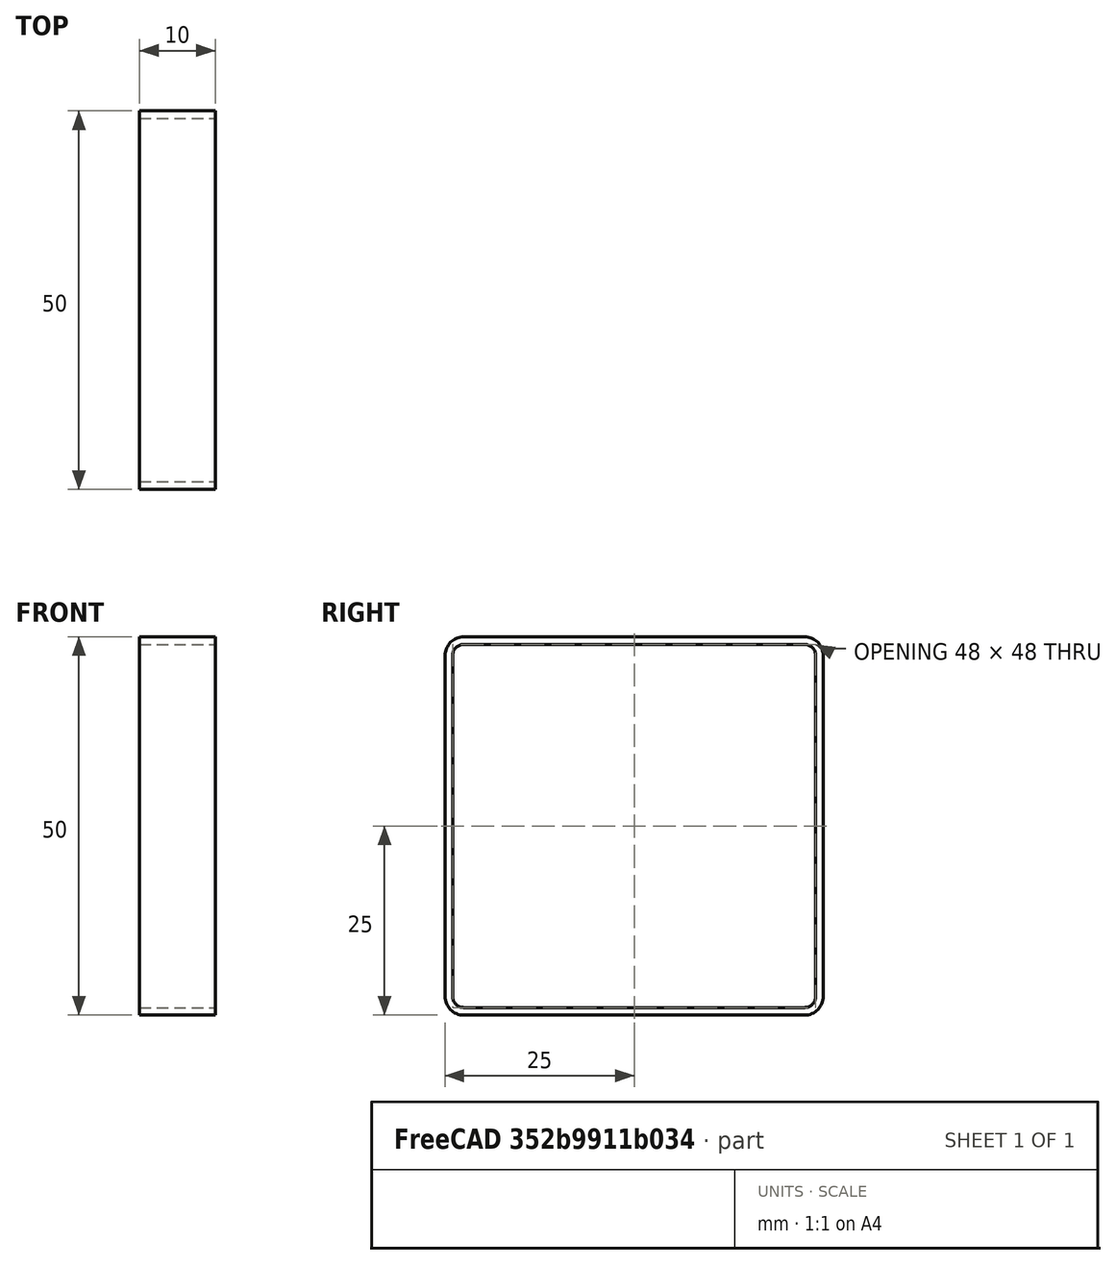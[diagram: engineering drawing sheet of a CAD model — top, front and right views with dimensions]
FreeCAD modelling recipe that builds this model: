
FCSTD DOCUMENT  (FreeCAD 0.20R26075 +2 (Git))
Label: Test6
License: All rights reserved
LicenseURL: http://en.wikipedia.org/wiki/All_rights_reserved
objects: Sketcher::SketchObject×1, PartDesign::Pad×1, PartDesign::Body×1
note: 4 computed .brp shape members not serialized (recipe doc carries the construction recipe); baked Part::Feature solids carry a one-line shape summary decoded from their .brp

FEATURE [Sketcher::SketchObject] Sketch
  FullyConstrained = true
  MapMode = 5
  Placement = pos=(0,0,0) rot=(0.57735,0.57735,0.57735;2.0944rad)
  Support = -> [YZ_Plane]
  sketch-geometry (20):
    g0: ArcOfCircle CenterX=-22.5 CenterY=22.5 CenterZ=0 NormalX=0 NormalY=0 NormalZ=1 AngleXU=0 Radius=2.5 StartAngle=1.5708 EndAngle=3.14159
    g1: LineSegment StartX=-22.5 StartY=25 StartZ=0 EndX=22.5 EndY=25 EndZ=0
    g2: ArcOfCircle CenterX=22.5 CenterY=22.5 CenterZ=0 NormalX=0 NormalY=0 NormalZ=1 AngleXU=0 Radius=2.5 StartAngle=0 EndAngle=1.5708
    g3: LineSegment StartX=25 StartY=22.5 StartZ=0 EndX=25 EndY=-22.5 EndZ=0
    g4: ArcOfCircle CenterX=22.5 CenterY=-22.5 CenterZ=0 NormalX=0 NormalY=0 NormalZ=1 AngleXU=0 Radius=2.5 StartAngle=4.71239 EndAngle=6.28319
    g5: LineSegment StartX=22.5 StartY=-25 StartZ=0 EndX=-22.5 EndY=-25 EndZ=0
    g6: ArcOfCircle CenterX=-22.5 CenterY=-22.5 CenterZ=0 NormalX=0 NormalY=0 NormalZ=1 AngleXU=0 Radius=2.5 StartAngle=3.14159 EndAngle=4.71239
    g7: LineSegment StartX=-25 StartY=-22.5 StartZ=0 EndX=-25 EndY=22.5 EndZ=0
    g8: GeomPoint X=-25 Y=25 Z=0
    g9: GeomPoint X=25 Y=-25 Z=0
    g10: ArcOfCircle CenterX=-22.5 CenterY=22.5 CenterZ=0 NormalX=0 NormalY=0 NormalZ=1 AngleXU=0 Radius=1.5 StartAngle=1.5708 EndAngle=3.14159
    g11: LineSegment StartX=-22.5 StartY=24 StartZ=0 EndX=22.5 EndY=24 EndZ=0
    g12: ArcOfCircle CenterX=22.5 CenterY=22.5 CenterZ=0 NormalX=0 NormalY=0 NormalZ=1 AngleXU=0 Radius=1.5 StartAngle=-2.958e-13 EndAngle=1.5708
    g13: LineSegment StartX=24 StartY=22.5 StartZ=0 EndX=24 EndY=-22.5 EndZ=0
    g14: ArcOfCircle CenterX=22.5 CenterY=-22.5 CenterZ=0 NormalX=0 NormalY=0 NormalZ=1 AngleXU=0 Radius=1.5 StartAngle=4.71239 EndAngle=6.28319
    g15: LineSegment StartX=22.5 StartY=-24 StartZ=0 EndX=-22.5 EndY=-24 EndZ=0
    g16: ArcOfCircle CenterX=-22.5 CenterY=-22.5 CenterZ=0 NormalX=0 NormalY=0 NormalZ=1 AngleXU=0 Radius=1.5 StartAngle=3.14159 EndAngle=4.71239
    g17: LineSegment StartX=-24 StartY=-22.5 StartZ=0 EndX=-24 EndY=22.5 EndZ=0
    g18: GeomPoint X=-24 Y=24 Z=0
    g19: GeomPoint X=24 Y=-24 Z=0
  constraints (45):
    c: Tangent(g0,g1) = 1.5708
    c: Tangent(g1,g2) = 1.5708
    c: Tangent(g2,g3) = 1.5708
    c: Tangent(g3,g4) = 1.5708
    c: Tangent(g4,g5) = 1.5708
    c: Tangent(g5,g6) = 1.5708
    c: Tangent(g6,g7) = 1.5708
    c: Tangent(g7,g0) = 1.5708
    c: Horizontal(g1)
    c: Horizontal(g5)
    c: Vertical(g3)
    c: Vertical(g7)
    c: Equal(g0,g2)
    c: Equal(g2,g4)
    c: Equal(g4,g6)
    c: PointOnObject(g8,g1)
    c: PointOnObject(g8,g7)
    c: PointOnObject(g9,g3)
    c: PointOnObject(g9,g5)
    c: Radius(g0) = 2.5
    c: DistanceX(g0,g2) = 50
    c: Equal(g1,g3)
    c: Symmetric(g0,g4,g-1)
    c: Tangent(g10,g11) = 1.5708
    c: Tangent(g11,g12) = 1.5708
    c: Tangent(g12,g13) = 1.5708
    c: Tangent(g13,g14) = 1.5708
    c: Tangent(g14,g15) = 1.5708
    c: Tangent(g15,g16) = 1.5708
    c: Tangent(g16,g17) = 1.5708
    c: Tangent(g17,g10) = 1.5708
    c: Horizontal(g11)
    c: Horizontal(g15)
    c: Vertical(g13)
    c: Vertical(g17)
    c: Equal(g10,g12)
    c: Equal(g12,g14)
    c: Equal(g14,g16)
    c: PointOnObject(g18,g11)
    c: PointOnObject(g18,g17)
    c: PointOnObject(g19,g13)
    c: PointOnObject(g19,g15)
    c: DistanceX(g6,g16) = 1
    c: Coincident(g16,g6)
    c: Coincident(g12,g2)
FEATURE [PartDesign::Pad] Pad
  Direction = (1,-2e-16,3e-16)
  Length = 10
  Length2 = 100
  Midplane = true
  Placement = pos=(0,0,0) rot=(0.57735,0.57735,0.57735;2.0944rad)
  Profile = -> Sketch
  Type = 0
FEATURE [PartDesign::Body] Body
  Group = -> [Sketch,Pad]
  Origin = -> Origin
  Tip = -> Pad
